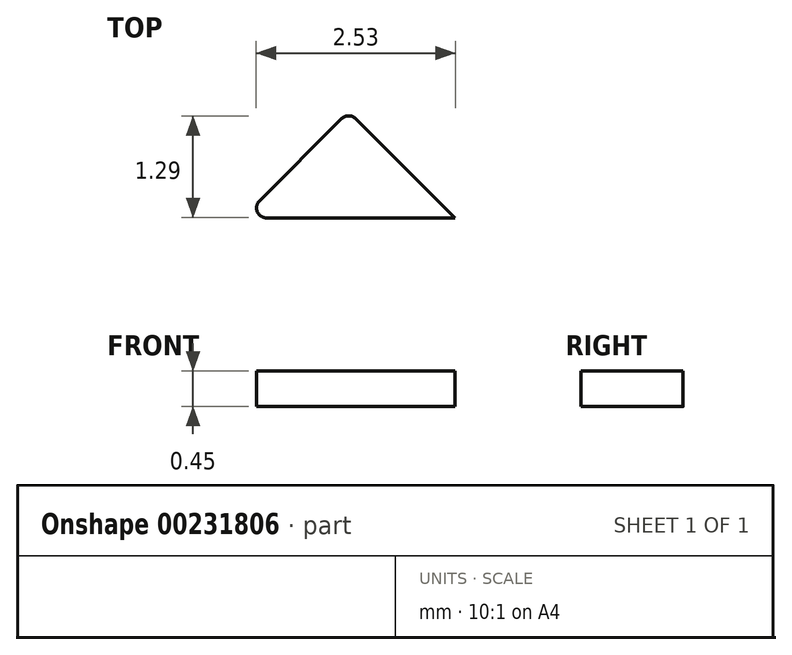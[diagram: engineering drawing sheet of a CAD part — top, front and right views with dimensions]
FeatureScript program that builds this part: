
annotation { "Feature Type Name" : "Feature", "Feature Type Description" : "" }
export const myFeature = defineFeature(function(context is Context, id is Id, definition is map)
    precondition{}
    {
        {
            var Q0;
            Q0=qCreatedBy(makeId("Top.planeOp"),FACE);
            var sketch = newSketch(context, id + "F0", { "sketchPlane" : qUnion([Q0])});
            skLineSegment(sketch, "E0.bottom", {"start": v(-96.31, 6.93) * mm, "end": v(-93.61, 6.93) * mm});
            skLineSegment(sketch, "E0.top", {"start": v(-96.31, 3.73) * mm, "end": v(-93.61, 3.73) * mm});
            skLineSegment(sketch, "E0.left", {"start": v(-96.31, 6.93) * mm, "end": v(-96.31, 3.73) * mm});
            skLineSegment(sketch, "E0.right", {"start": v(-93.61, 6.93) * mm, "end": v(-93.61, 3.73) * mm});
            skSolve(sketch);
        }
        {
            var Q0;
            Q0=makeQuery(id+"F0.imprint","IMPRINT",FACE,{"disambiguationData":[TD([[makeQuery(id+"F0.imprint","IMPRINT",EDGE,{"derivedFrom":sQuery(id+"F0.wireOp",EDGE,"E0.bottom")}),-1.0]])]});
            extrude(context, id + "F1", {"entities" : qUnion([Q0]), "depth" : .45 * mm});
        }
        {
            var Q0;
            Q0=makeQuery(id+"F1.opExtrude","SWEPT_EDGE",EDGE,{"disambiguationData":[OSD([sQuery(id+"F0.wireOp",EDGE,"E0.top"),sQuery(id+"F0.wireOp",EDGE,"E0.left")])]});
            var Q1;
            Q1=makeQuery(id+"F1.opExtrude","SWEPT_EDGE",EDGE,{"disambiguationData":[OSD([sQuery(id+"F0.wireOp",EDGE,"E0.bottom"),sQuery(id+"F0.wireOp",EDGE,"E0.left")])]});
            var Q2;
            Q2=makeQuery(id+"F1.opExtrude","SWEPT_EDGE",EDGE,{"disambiguationData":[OSD([sQuery(id+"F0.wireOp",EDGE,"E0.bottom"),sQuery(id+"F0.wireOp",EDGE,"E0.right")])]});
            var Q3;
            Q3=makeQuery(id+"F1.opExtrude","SWEPT_EDGE",EDGE,{"disambiguationData":[OSD([sQuery(id+"F0.wireOp",EDGE,"E0.top"),sQuery(id+"F0.wireOp",EDGE,"E0.right")])]});
            chamfer(context, id + "F2", {"entities" : qUnion([Q0, Q1, Q2, Q3]), "width" : 1.57 * mm, "tangentPropagation" : true});
        }
        {
            var Q0;
            Q0=makeQuery(id+"F1.opExtrude","SWEPT_FACE",FACE,{"disambiguationData":[OSD([sQuery(id+"F0.wireOp",EDGE,"E0.left")])]});
            extrude(context, id + "F3", {"entities" : qUnion([Q0]), "operationType" : NewBodyOperationType.REMOVE, "oppositeDirection" : true, "depth" : 25.4 * mm});
        }
        {
            var Q0;
            Q0=makeQuery(id+"F3.boolean.opBoolean","COPY",FACE,{"derivedFrom":makeQuery(id+"F3.opExtrude","SWEPT_FACE",FACE,{"disambiguationData":[OSD([sQuery(id+"F0.wireOp",EDGE,"E0.top"),sQuery(id+"F0.wireOp",EDGE,"E0.left")])]})});
            extrude(context, id + "F4", {"entities" : qUnion([Q0]), "operationType" : NewBodyOperationType.REMOVE, "oppositeDirection" : true, "depth" : 25.4 * mm});
        }
        {
            var Q0;
            {var subQ0=sQuery(id+"F0.wireOp",EDGE,"E0.bottom");Q0=makeQuery(id+"F2.opChamfer","BLEND_EDGE",EDGE,{"blendedFrom":[makeQuery(id+"F1.opExtrude","SWEPT_EDGE",EDGE,{"disambiguationData":[OSD([subQ0,sQuery(id+"F0.wireOp",EDGE,"E0.left")])]}),makeQuery(id+"F1.opExtrude","SWEPT_EDGE",EDGE,{"disambiguationData":[OSD([subQ0,sQuery(id+"F0.wireOp",EDGE,"E0.right")])]})],"blendedInto":[]});}
            var Q1;
            {var subQ0=sQuery(id+"F0.wireOp",EDGE,"E0.right");Q1=makeQuery(id+"F2.opChamfer","BLEND_EDGE",EDGE,{"blendedFrom":[makeQuery(id+"F1.opExtrude","SWEPT_EDGE",EDGE,{"disambiguationData":[OSD([sQuery(id+"F0.wireOp",EDGE,"E0.bottom"),subQ0])]}),makeQuery(id+"F1.opExtrude","SWEPT_FACE",FACE,{"disambiguationData":[OSD([subQ0])]})],"blendedInto":[makeQuery(id+"F1.opExtrude","SWEPT_FACE",FACE,{"disambiguationData":[OSD([subQ0])]})]});}
            var Q2;
            {var subQ0=sQuery(id+"F0.wireOp",EDGE,"E0.left");var subQ1=sQuery(id+"F0.wireOp",EDGE,"E0.bottom");Q2=makeQuery(id+"F3.boolean.opBoolean","MERGE",EDGE,{"derivedFrom":[makeQuery(id+"F2.opChamfer","BLEND_EDGE",EDGE,{"blendedFrom":[makeQuery(id+"F1.opExtrude","SWEPT_EDGE",EDGE,{"disambiguationData":[OSD([subQ1,subQ0])]}),makeQuery(id+"F1.opExtrude","SWEPT_FACE",FACE,{"disambiguationData":[OSD([subQ0])]})],"blendedInto":[makeQuery(id+"F1.opExtrude","SWEPT_FACE",FACE,{"disambiguationData":[OSD([subQ0])]})]}),makeQuery(id+"F3.opExtrude","CAP_EDGE",EDGE,{"disambiguationData":[OSD([subQ1,subQ0])],"isStart":true})]});}
            fillet(context, id + "F5", {"entities" : qUnion([Q0, Q1, Q2]), "radius" : 0.13 * mm, "tangentPropagation" : true, "allowEdgeOverflow" : false});
        }
    });
